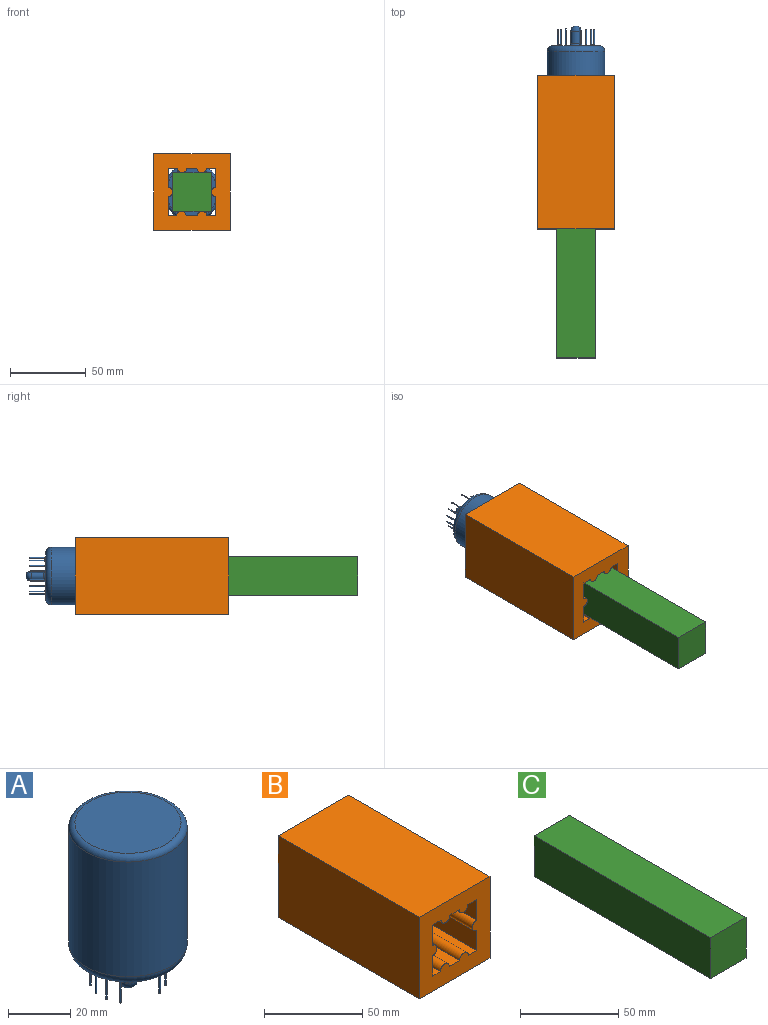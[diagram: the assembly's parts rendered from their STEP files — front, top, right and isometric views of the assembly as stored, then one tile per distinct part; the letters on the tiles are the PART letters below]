
ASSEMBLY  parts=3 mates=2
PART A: 49 faces, bbox 41.1x41.1x64 mm
  f0: plane 34x34mm, normal (0,0,1), area 907.9mm2, adj f7
  f1: sphere r=3.5mm, area 77mm2, adj f2
  f2: cylinder r=3.5mm len=8mm, axis (0,0,-1), area 175.9mm2, adj f1,f3
  f3: torus R=5mm, axis (0,0,-1), area 59.9mm2, adj f2,f4
  f4: plane 30x30mm, normal (0,0,-1), area 582.4mm2, adj f3,f5,f8,f11,f14,f17,f20,f23
  f5: torus R=15mm, axis (0,0,-1), area 692.7mm2, adj f4,f6
  f6: cylinder r=19mm len=45mm, axis (0,0,-1), area 5372.1mm2, adj f5,f7
  f7: torus R=17mm, axis (0,0,-1), area 360.7mm2, adj f0,f6
  f8: torus R=1.15mm, axis (0,0,1), area 5.1mm2, adj f4,f9
  f9: cylinder r=0.3mm len=10.14mm, axis (0,0,1), area 18.9mm2, adj f8,f10
  f10: plane 0.59x0.59mm, normal (0,0,-1), area 0.3mm2, adj f9
  f11: torus R=1.15mm, axis (0,0,1), area 5.1mm2, adj f4,f12
  f12: cylinder r=0.3mm len=10.14mm, axis (0,0,1), area 18.9mm2, adj f11,f13
  f13: plane 0.59x0.59mm, normal (0,0,-1), area 0.3mm2, adj f12
  f14: torus R=1.15mm, axis (0,0,1), area 5.1mm2, adj f4,f15
  f15: cylinder r=0.3mm len=10.14mm, axis (0,0,1), area 18.9mm2, adj f14,f16
  f16: plane 0.59x0.59mm, normal (0,0,-1), area 0.3mm2, adj f15
  f17: torus R=1.15mm, axis (0,0,1), area 5.1mm2, adj f4,f18
  f18: cylinder r=0.3mm len=10.14mm, axis (0,0,1), area 18.9mm2, adj f17,f19
  f19: plane 0.59x0.59mm, normal (0,0,-1), area 0.3mm2, adj f18
  f20: torus R=1.15mm, axis (0,0,1), area 5.1mm2, adj f4,f21
  f21: cylinder r=0.3mm len=10.14mm, axis (0,0,1), area 18.9mm2, adj f20,f22
  f22: plane 0.59x0.59mm, normal (0,0,-1), area 0.3mm2, adj f21
  f23: torus R=1.15mm, axis (0,0,1), area 5.1mm2, adj f4,f24
  f24: cylinder r=0.3mm len=10.14mm, axis (0,0,1), area 18.9mm2, adj f23,f25
  f25: plane 0.59x0.59mm, normal (0,0,-1), area 0.3mm2, adj f24
  f26: torus R=1.15mm, axis (0,0,1), area 5.1mm2, adj f4,f27
  f27: cylinder r=0.3mm len=10.14mm, axis (0,0,1), area 18.9mm2, adj f26,f28
  f28: plane 0.59x0.59mm, normal (0,0,-1), area 0.3mm2, adj f27
  f29: torus R=1.15mm, axis (0,0,1), area 5.1mm2, adj f4,f30
  f30: cylinder r=0.3mm len=10.14mm, axis (0,0,1), area 18.9mm2, adj f29,f31
  f31: plane 0.59x0.59mm, normal (0,0,-1), area 0.3mm2, adj f30
  f32: torus R=1.15mm, axis (0,0,1), area 5.1mm2, adj f4,f33
  f33: cylinder r=0.3mm len=10.14mm, axis (0,0,1), area 18.9mm2, adj f32,f34
  f34: plane 0.59x0.59mm, normal (0,0,-1), area 0.3mm2, adj f33
  f35: torus R=1.15mm, axis (0,0,1), area 5.1mm2, adj f4,f36
  f36: cylinder r=0.3mm len=10.14mm, axis (0,0,1), area 18.9mm2, adj f35,f37
  f37: plane 0.59x0.59mm, normal (0,0,-1), area 0.3mm2, adj f36
  f38: torus R=1.15mm, axis (0,0,1), area 5.1mm2, adj f4,f39
  f39: cylinder r=0.3mm len=10.14mm, axis (0,0,1), area 18.9mm2, adj f38,f40
  f40: plane 0.59x0.59mm, normal (0,0,-1), area 0.3mm2, adj f39
  f41: plane 20x20mm, normal (0,0,1), area 235.6mm2, adj f42,f48
  f42: torus R=5mm, axis (0,0,1), area 95.7mm2, adj f41,f43
  f43: cylinder r=1.5mm len=8mm, axis (0,0,1), area 75.4mm2, adj f42,f44
  f44: sphere r=1.5mm, area 14.1mm2, adj f43
  f45: plane 20x20mm, normal (0,0,-1), area 314.2mm2, adj f46
  f46: torus R=10mm, axis (0,0,1), area 998.8mm2, adj f45,f47
  f47: cylinder r=17mm len=34mm, axis (0,0,1), area 3524.9mm2, adj f46,f48
  f48: torus R=10mm, axis (0,0,1), area 998.8mm2, adj f41,f47
PART B: 36 faces, bbox 50.8x101.6x50.8 mm
  f0: cylinder r=22.23mm len=51.31mm, axis (0,1,0), area 2061.7mm2, adj f5,f6,f11,f12,f13,f17,f18,f19
  f1: cylinder r=22.23mm len=51.31mm, axis (0,1,0), area 2062mm2, adj f4,f6,f11,f14,f16,f19,f21,f23
  f2: cylinder r=22.23mm len=51.31mm, axis (0,1,0), area 2062mm2, adj f4,f5,f11,f15,f16,f17,f21,f22
  f3: plane 50.8x50.8mm, normal (0,-1,0), area 1667.6mm2, adj f7,f8,f9,f10,f16,f17,f18,f19
  f4: plane 31.11x6.12mm, normal (0,1,0), area 120.6mm2, adj f1,f2,f16,f21
  f5: plane 31.11x6.35mm, normal (0,1,0), area 120.6mm2, adj f0,f2,f17,f22
  f6: plane 31.11x6.35mm, normal (0,1,0), area 120.6mm2, adj f0,f1,f19,f23
  f7: plane 101.6x50.8mm, normal (0,0,1), area 5161.3mm2, adj f3,f8,f10,f11
  f8: plane 101.6x50.8mm, normal (-1,0,0), area 5161.3mm2, adj f3,f7,f9,f11
  f9: plane 101.6x50.8mm, normal (0,0,-1), area 5161.3mm2, adj f3,f8,f10,f11
  f10: plane 101.6x50.8mm, normal (1,0,0), area 5161.3mm2, adj f3,f7,f9,f11
  f11: plane 50.8x50.8mm, normal (0,1,0), area 1074.9mm2, adj f0,f1,f2,f7,f8,f9,f10,f21
  f12: plane 31.11x6.35mm, normal (0,1,0), area 136mm2, adj f0,f18
  f13: plane 0.32x0.32mm, normal (0,-1,0), area 0.1mm2, adj f0,f18,f19
  f14: plane 0.32x0.32mm, normal (0,-1,0), area 0.1mm2, adj f1,f16,f19
  f15: plane 0.32x0.32mm, normal (0,-1,0), area 0.1mm2, adj f2,f16,f17
  f16: plane 50.8x31.75mm, normal (0,0,-1), area 984.2mm2, adj f1,f2,f3,f4,f14,f15,f17,f19
  f17: plane 50.8x31.75mm, normal (1,0,0), area 1290.6mm2, adj f0,f2,f3,f5,f15,f16,f18,f20
  f18: plane 50.8x31.75mm, normal (0,0,1), area 984.2mm2, adj f0,f3,f12,f13,f17,f19,f20,f24
  f19: plane 50.8x31.75mm, normal (-1,0,0), area 1290.6mm2, adj f0,f1,f3,f6,f13,f14,f16,f18
  f20: plane 0.32x0.32mm, normal (0,-1,0), area 0.1mm2, adj f0,f17,f18
  f21: cylinder r=3.17mm len=51.31mm, axis (0,1,0), area 488.5mm2, adj f1,f2,f4,f11
  f22: cylinder r=3.17mm len=51.31mm, axis (0,1,0), area 488.5mm2, adj f0,f2,f5,f11
  f23: cylinder r=3.17mm len=51.31mm, axis (0,1,0), area 488.5mm2, adj f0,f1,f6,f11
  f24: cylinder r=3.17mm len=48.26mm, axis (0,-1,0), area 481.4mm2, adj f3,f18,f25
  f25: plane 6.35x3.18mm, normal (0,1,0), area 15.8mm2, adj f18,f24
  f26: cylinder r=3.17mm len=48.26mm, axis (0,-1,0), area 481.4mm2, adj f3,f18,f27
  f27: plane 6.35x3.18mm, normal (0,1,0), area 15.8mm2, adj f18,f26
  f28: cylinder r=3.17mm len=48.26mm, axis (0,-1,0), area 481.4mm2, adj f3,f19,f29
  f29: plane 6.35x3.18mm, normal (0,1,0), area 15.8mm2, adj f19,f28
  f30: cylinder r=3.17mm len=48.26mm, axis (0,-1,0), area 481.4mm2, adj f3,f16,f31
  f31: plane 6.35x3.18mm, normal (0,1,0), area 15.8mm2, adj f16,f30
  f32: cylinder r=3.17mm len=48.26mm, axis (0,-1,0), area 481.4mm2, adj f3,f16,f33
  f33: plane 6.35x3.18mm, normal (0,1,0), area 15.8mm2, adj f16,f32
  f34: cylinder r=3.17mm len=48.26mm, axis (0,-1,0), area 481.4mm2, adj f3,f17,f35
  f35: plane 6.35x3.18mm, normal (0,1,0), area 15.8mm2, adj f17,f34
PART C: 6 faces, bbox 25.4x127x25.4 mm
  f0: plane 127x25.4mm, normal (0,0,1), area 3225.8mm2, adj f1,f3,f4,f5
  f1: plane 127x25.4mm, normal (-1,0,0), area 3225.8mm2, adj f0,f2,f4,f5
  f2: plane 127x25.4mm, normal (0,0,-1), area 3225.8mm2, adj f1,f3,f4,f5
  f3: plane 127x25.4mm, normal (1,0,0), area 3225.8mm2, adj f0,f2,f4,f5
  f4: plane 25.4x25.4mm, normal (0,-1,0), area 645.2mm2, adj f0,f1,f2,f3
  f5: plane 25.4x25.4mm, normal (0,1,0), area 645.2mm2, adj f0,f1,f2,f3
PLACE A rot(axis=(1,0,0),90deg) t=(-35.49,-0.95,-0.23)mm
PLACE B t=(-35.49,-20.65,-0.23)mm fixed
PLACE C t=(-35.51,-80.62,-0.23)mm
MATE slider A.f2 <-> B.f0  axis (0,-1,0) through (-35.49,-51.95,-0.23)mm
MATE slider B.f3 <-> C.f4  axis (0,-1,0) through (-35.51,-122.25,-0.23)mm
